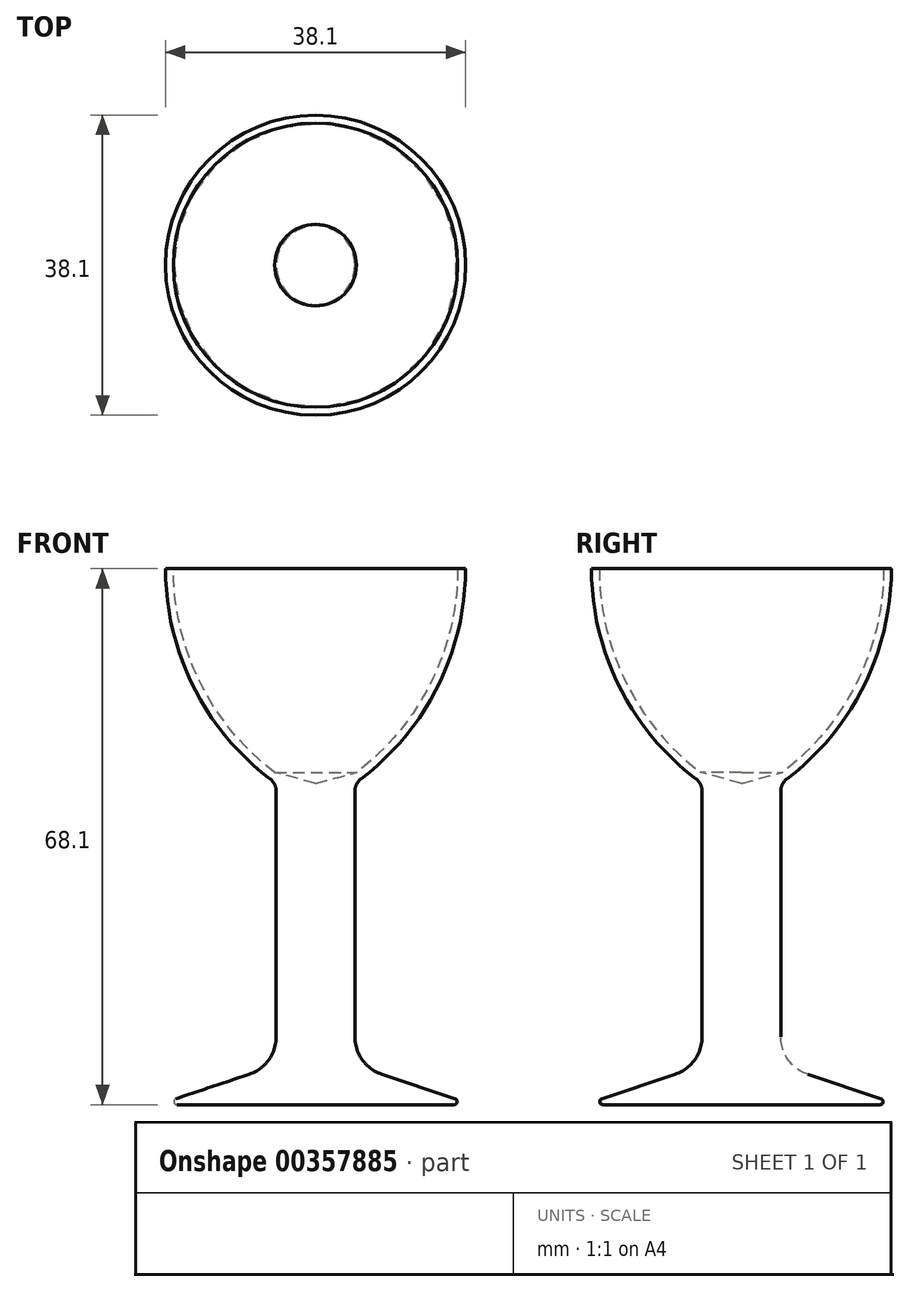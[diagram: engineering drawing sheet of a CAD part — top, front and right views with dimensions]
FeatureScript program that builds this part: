
annotation { "Feature Type Name" : "Feature", "Feature Type Description" : "" }
export const myFeature = defineFeature(function(context is Context, id is Id, definition is map)
    precondition{}
    {
        {
            var Q0;
            Q0=qCreatedBy(makeId("Front.planeOp"),FACE);
            var sketch = newSketch(context, id + "F0", { "sketchPlane" : qUnion([Q0])});
            skLineSegment(sketch, "E0.bottom", {"start": v(0, 0) * mm, "end": v(17.61, 0) * mm});
            skLineSegment(sketch, "E0.left", {"start": v(0, 0) * mm, "end": v(0, 40.82) * mm});
            skLineSegment(sketch, "E1.0", {"start": v(5, 8.6) * mm, "end": v(5, 39.8) * mm});
            skLineSegment(sketch, "E2", {"start": v(8.42, 3.86) * mm, "end": v(17.73, 0.76) * mm});
            skArc(sketch, "E3", {"start": v(5.8, 41.4) * mm, "mid": v(15.56, 53.2) * mm, "end": v(19.05, 68.1) * mm});
            skPoint(sketch, "E4.visualSharp", {"position": v(5, 5) * mm});
            skArc(sketch, "E4.filletArc", {"start": v(5, 8.6) * mm, "mid": v(5.94, 5.68) * mm, "end": v(8.42, 3.86) * mm});
            skPoint(sketch, "E5.visualSharp", {"position": v(20, 0) * mm});
            skArc(sketch, "E5.filletArc", {"start": v(17.61, 0) * mm, "mid": v(18, 0.33) * mm, "end": v(17.73, 0.76) * mm});
            skArc(sketch, "E6.filletArc", {"start": v(5.8, 41.4) * mm, "mid": v(5.2, 40.7) * mm, "end": v(5, 39.8) * mm});
            skArc(sketch, "E7.0", {"start": v(5.19, 42.2) * mm, "mid": v(14.66, 53.64) * mm, "end": v(18.05, 68.1) * mm});
            skLineSegment(sketch, "E8", {"start": v(5.19, 42.2) * mm, "end": v(0, 40.82) * mm});
            skLineSegment(sketch, "E9", {"start": v(18.05, 68.1) * mm, "end": v(19.05, 68.1) * mm});
            skSolve(sketch);
        }
        {
            var Q0;
            Q0=makeQuery(id+"F0.imprint","IMPRINT",FACE,{"disambiguationData":[TD([[makeQuery(id+"F0.imprint","IMPRINT",EDGE,{"derivedFrom":sQuery(id+"F0.wireOp",EDGE,"E0.bottom")}),1.0]])]});
            var Q1;
            Q1=sQuery(id+"F0.wireOp",EDGE,"E0.left");
            revolve(context, id + "F1", {"entities" : qUnion([Q0]), "axis" : qUnion([Q1]), "revolveType" : RevolveType.FULL});
        }
    });
